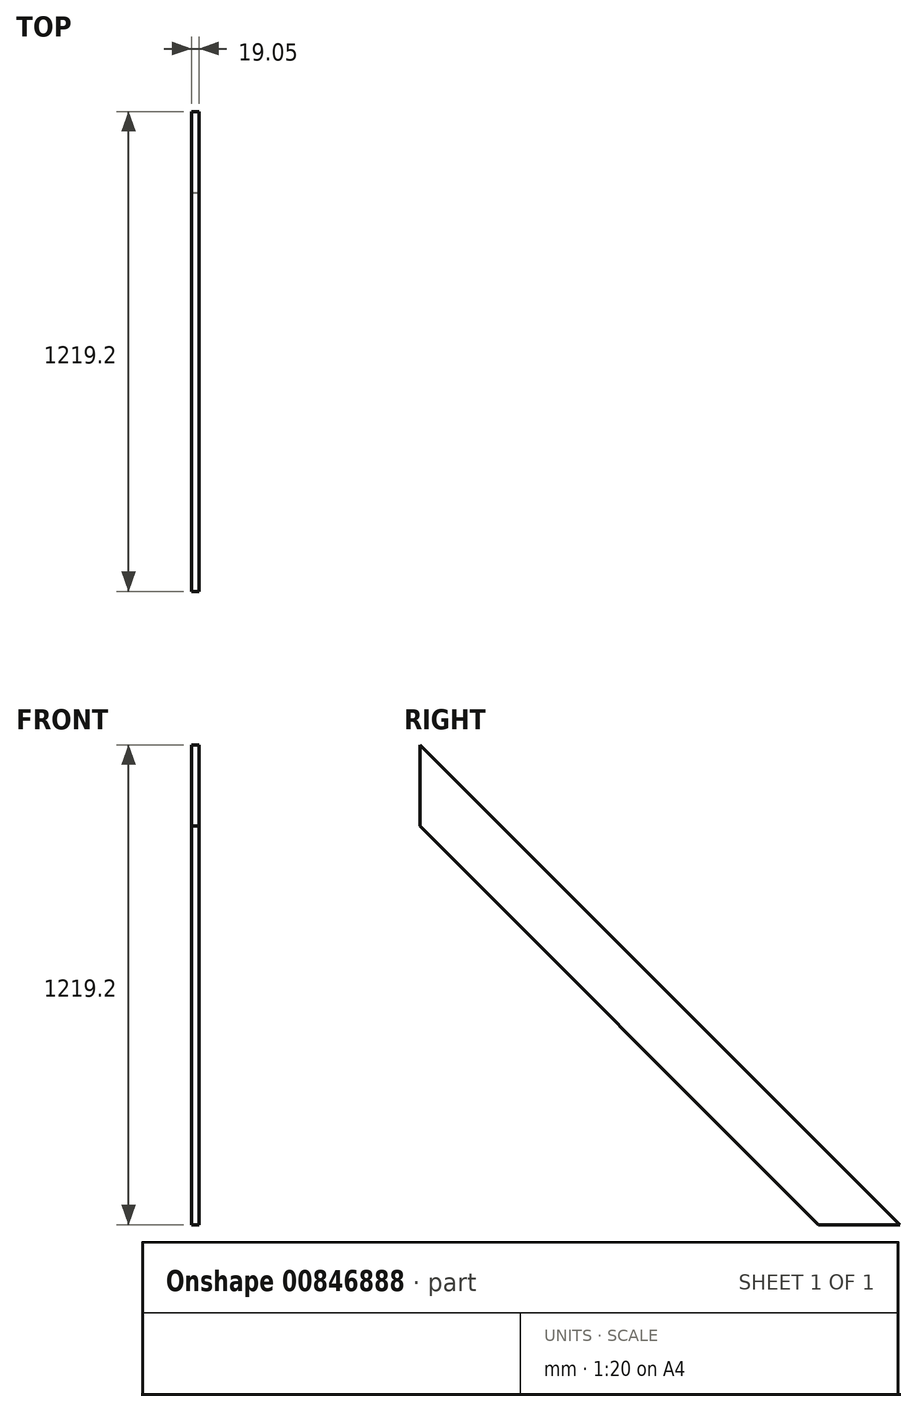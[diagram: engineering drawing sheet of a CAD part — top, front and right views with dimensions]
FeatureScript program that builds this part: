
annotation { "Feature Type Name" : "Feature", "Feature Type Description" : "" }
export const myFeature = defineFeature(function(context is Context, id is Id, definition is map)
    precondition{}
    {
        {
            var Q0;
            Q0=qCreatedBy(makeId("Right.planeOp"),FACE);
            var sketch = newSketch(context, id + "F0", { "sketchPlane" : qUnion([Q0])});
            skLineSegment(sketch, "E0", {"start": v(0, 0) * mm, "end": v(1219.2, -1219.2) * mm});
            skLineSegment(sketch, "E1", {"start": v(1219.2, -1219.2) * mm, "end": v(1012.65, -1219.2) * mm});
            skLineSegment(sketch, "E2", {"start": v(1012.65, -1219.2) * mm, "end": v(0, -206.55) * mm});
            skLineSegment(sketch, "E3", {"start": v(0, -206.55) * mm, "end": v(0, 0) * mm});
            skSolve(sketch);
        }
        {
            var Q0;
            Q0=makeQuery(id+"F0.imprint","IMPRINT",FACE,{"disambiguationData":[TD([[makeQuery(id+"F0.imprint","IMPRINT",EDGE,{"derivedFrom":sQuery(id+"F0.wireOp",EDGE,"E0")}),-1.0]])]});
            extrude(context, id + "F1", {"entities" : qUnion([Q0]), "oppositeDirection" : true, "depth" : 19.05 * mm, "offsetDistance" : 25.4 * mm});
        }
    });
